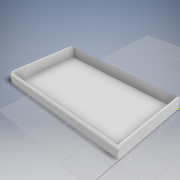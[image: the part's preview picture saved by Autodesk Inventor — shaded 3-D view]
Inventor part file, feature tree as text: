
AUTODESK INVENTOR PART (.ipt)
format: ipt  version: 2018 (Build 220112000, 112)  size: 133,120 bytes
history: native  units: in
note: dims shown in document units (in); Inventor stores cm internally (conversion verified against a paired STEP export)
features: sketch x4, fillet x4, extrude x2
ambient origin geometry x8: Origin, YZ Plane, XZ Plane, XY Plane, X Axis, Y Axis, Z Axis, Center Point
bodies: Solid1 (feature_tree)
feature tree (10):
  extrude  "Extrusion1"  Depth=2.9528in
  sketch  "Sketch2"  dims[d2=0.0394in d3=0.0in d4=0.0591in d5=0.0591in d6=4.8031in d7=2.8346in d8=0.5118in d9=0.0in]
  sketch  "Sketch3"  dims[d10=0.1575in]
  extrude  "Extrusion2"  Depth=0.0591in
  fillet  "Fillet1"  Radius=0.0591in
  fillet  "Fillet2"  Radius=4.8031in
  fillet  "Fillet3"  Radius=2.8346in
  fillet  "Fillet4"  Radius=0.5118in
  sketch  "Sketch1"  dims[d0=4.9213in d1=2.9528in]
  sketch  "Sketch4"  dims[d11=0.1575in d12=0.1575in d13=0.1575in]
